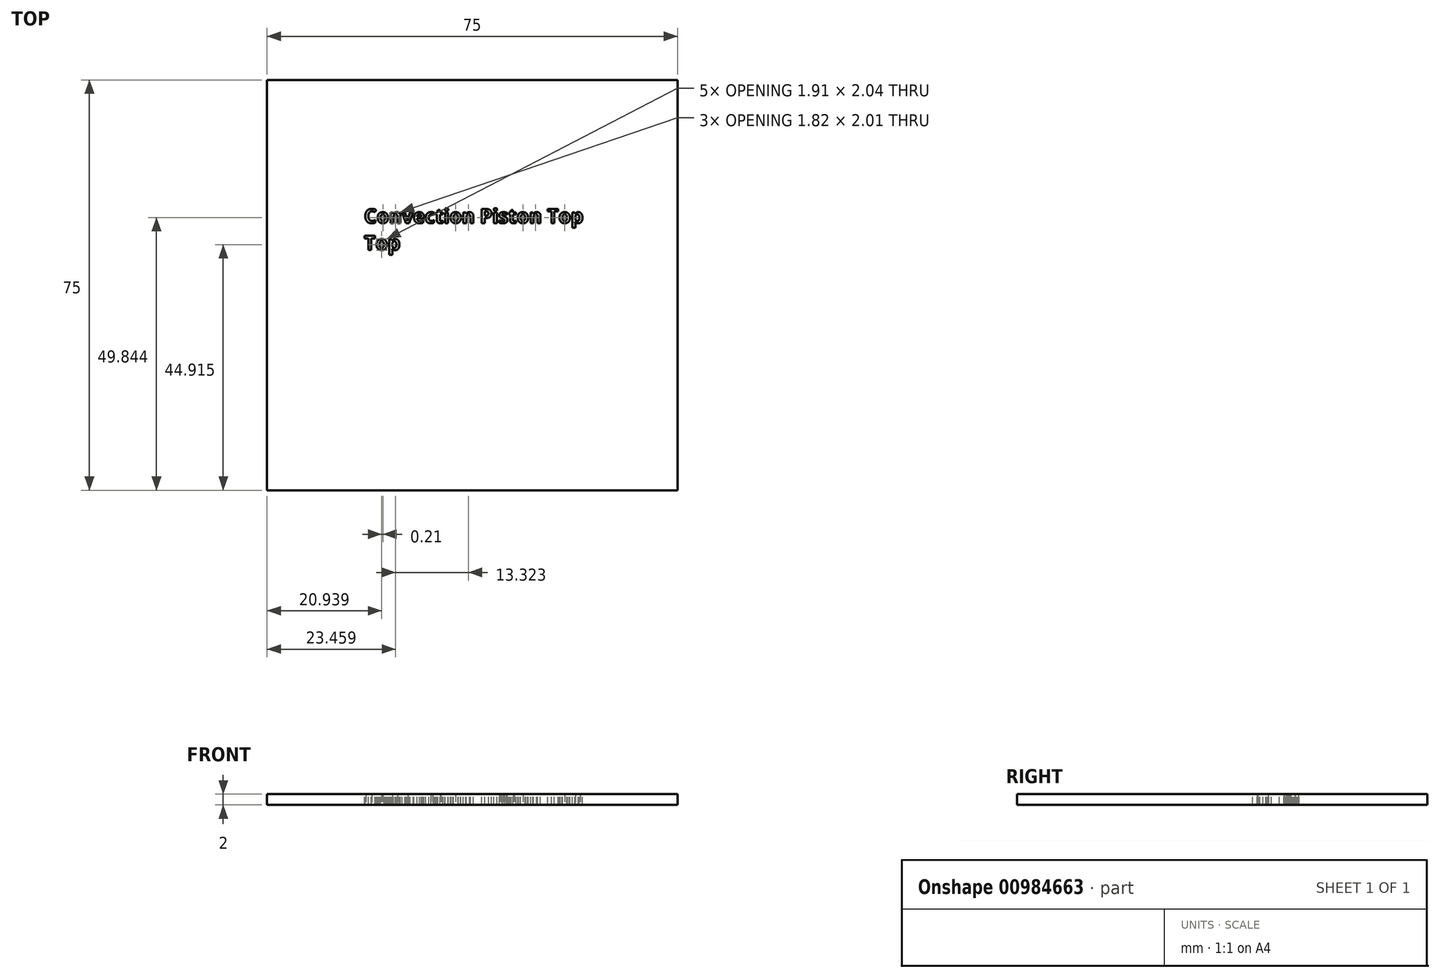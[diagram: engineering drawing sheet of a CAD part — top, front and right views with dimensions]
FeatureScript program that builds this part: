
annotation { "Feature Type Name" : "Feature", "Feature Type Description" : "" }
export const myFeature = defineFeature(function(context is Context, id is Id, definition is map)
    precondition{}
    {
        {
            var Q0;
            Q0=qCreatedBy(makeId("Top.planeOp"),FACE);
            var sketch = newSketch(context, id + "F0", { "sketchPlane" : qUnion([Q0])});
            skLineSegment(sketch, "E0.bottom", {"start": v(-43.5, 41.65) * mm, "end": v(31.5, 41.65) * mm});
            skLineSegment(sketch, "E0.top", {"start": v(-43.5, -33.35) * mm, "end": v(31.5, -33.35) * mm});
            skLineSegment(sketch, "E0.left", {"start": v(-43.5, 41.65) * mm, "end": v(-43.5, -33.35) * mm});
            skLineSegment(sketch, "E0.right", {"start": v(31.5, 41.65) * mm, "end": v(31.5, -33.35) * mm});
            skSolve(sketch);
        }
        {
            var Q0;
            Q0 = qSketchRegion(id + "F0", true);
            extrude(context, id + "F1", {"entities" : qUnion([Q0]), "depth" : 2 * mm, "offsetDistance" : 25 * mm});
        }
        {
            var Q0;
            Q0=makeQuery(id+"F1.opExtrude","CAP_FACE",FACE,{"disambiguationData":[OSD([sQuery(id+"F0.wireOp",EDGE,"E0.bottom"),sQuery(id+"F0.wireOp",EDGE,"E0.top"),sQuery(id+"F0.wireOp",EDGE,"E0.left"),sQuery(id+"F0.wireOp",EDGE,"E0.right")])],"isStart":false});
            var sketch = newSketch(context, id + "F2", { "sketchPlane" : qUnion([Q0])});
            skText(sketch, "E1", { "text": "Convection Piston Top\nTop", "fontName": "OpenSans-Bold.ttf"});
            const initialGuessF2  = {"E1": [-0.02577, 0.01549, 1, 0, 0.0026]};
            skSetInitialGuess(sketch, initialGuessF2);
            skSolve(sketch);
        }
        {
            var Q0;
            Q0 = qSketchRegion(id + "F2", true);
            extrude(context, id + "F3", {"entities" : qUnion([Q0]), "operationType" : NewBodyOperationType.REMOVE, "oppositeDirection" : true, "depth" : 25 * mm, "offsetDistance" : 25 * mm});
        }
    });
